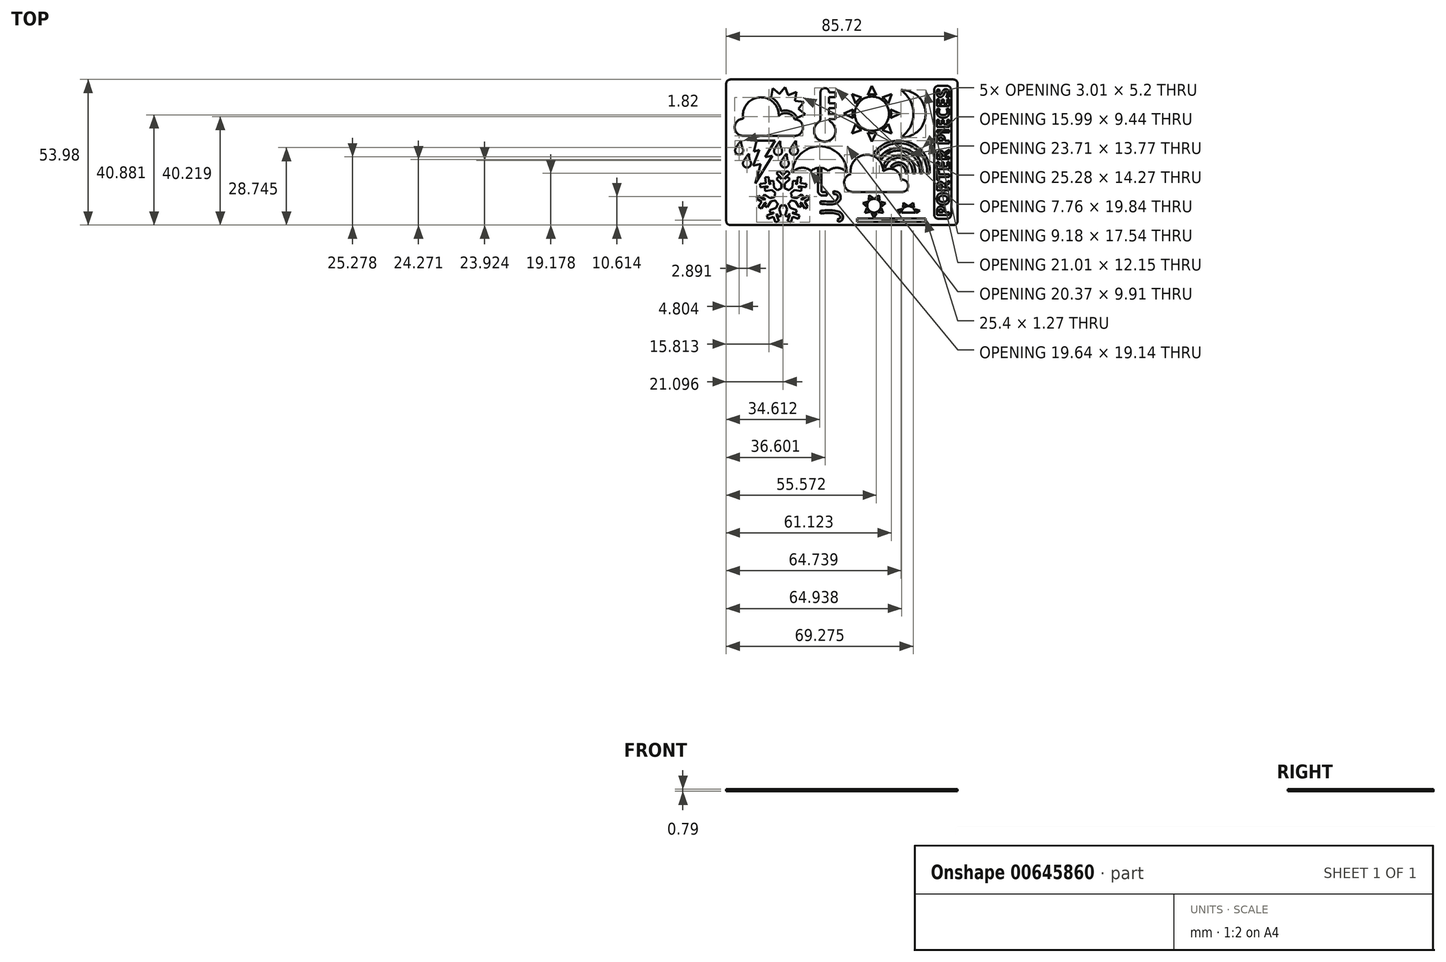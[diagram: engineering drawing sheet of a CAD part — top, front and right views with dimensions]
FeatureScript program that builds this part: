
annotation { "Feature Type Name" : "Feature", "Feature Type Description" : "" }
export const myFeature = defineFeature(function(context is Context, id is Id, definition is map)
    precondition{}
    {
        {
            var Q0;
            Q0=qCreatedBy(makeId("Top.planeOp"),FACE);
            var sketch = newSketch(context, id + "F0", { "sketchPlane" : qUnion([Q0])});
            skLineSegment(sketch, "E0.bottom", {"start": v(42.86, 26.99) * mm, "end": v(-42.86, 26.99) * mm});
            skLineSegment(sketch, "E0.top", {"start": v(42.86, -26.99) * mm, "end": v(-42.86, -26.99) * mm});
            skLineSegment(sketch, "E0.left", {"start": v(42.86, 26.99) * mm, "end": v(42.86, -26.99) * mm});
            skLineSegment(sketch, "E0.right", {"start": v(-42.86, 26.99) * mm, "end": v(-42.86, -26.99) * mm});
            skPoint(sketch, "E0.middle", {"position": v(0, 0) * mm});
            skSolve(sketch);
        }
        {
            var Q0;
            Q0=makeQuery(id+"F0.imprint","IMPRINT",FACE,{"disambiguationData":[TD([[makeQuery(id+"F0.imprint","IMPRINT",EDGE,{"derivedFrom":sQuery(id+"F0.wireOp",EDGE,"E0.bottom")}),1.0]])]});
            extrude(context, id + "F1", {"entities" : qUnion([Q0]), "depth" : 0.8 * mm, "offsetDistance" : 25.4 * mm});
        }
        {
            var Q0;
            Q0=makeQuery(id+"F1.opExtrude","SWEPT_EDGE",EDGE,{"disambiguationData":[OSD([sQuery(id+"F0.wireOp",EDGE,"E0.bottom"),sQuery(id+"F0.wireOp",EDGE,"E0.left")])]});
            var Q1;
            Q1=makeQuery(id+"F1.opExtrude","SWEPT_EDGE",EDGE,{"disambiguationData":[OSD([sQuery(id+"F0.wireOp",EDGE,"E0.bottom"),sQuery(id+"F0.wireOp",EDGE,"E0.right")])]});
            var Q2;
            Q2=makeQuery(id+"F1.opExtrude","SWEPT_EDGE",EDGE,{"disambiguationData":[OSD([sQuery(id+"F0.wireOp",EDGE,"E0.top"),sQuery(id+"F0.wireOp",EDGE,"E0.right")])]});
            var Q3;
            Q3=makeQuery(id+"F1.opExtrude","SWEPT_EDGE",EDGE,{"disambiguationData":[OSD([sQuery(id+"F0.wireOp",EDGE,"E0.top"),sQuery(id+"F0.wireOp",EDGE,"E0.left")])]});
            fillet(context, id + "F2", {"entities" : qUnion([Q0, Q1, Q2, Q3]), "radius" : 1.59 * mm, "tangentPropagation" : true, "allowEdgeOverflow" : false});
        }
        {
            var Q0;
            Q0=makeQuery(id+"F1.opExtrude","CAP_FACE",FACE,{"disambiguationData":[OSD([sQuery(id+"F0.wireOp",EDGE,"E0.bottom"),sQuery(id+"F0.wireOp",EDGE,"E0.top"),sQuery(id+"F0.wireOp",EDGE,"E0.left"),sQuery(id+"F0.wireOp",EDGE,"E0.right")])],"isStart":false});
            var sketch = newSketch(context, id + "F3", { "sketchPlane" : qUnion([Q0])});
            skLineSegment(sketch, "E1.bottom", {"start": v(34.13, -24.6) * mm, "end": v(40.48, -24.6) * mm});
            skLineSegment(sketch, "E1.top", {"start": v(34.13, 24.6) * mm, "end": v(40.48, 24.6) * mm});
            skLineSegment(sketch, "E1.left", {"start": v(34.13, -24.6) * mm, "end": v(34.13, 24.6) * mm});
            skLineSegment(sketch, "E1.right", {"start": v(40.48, -24.6) * mm, "end": v(40.48, 24.6) * mm});
            skSolve(sketch);
        }
        {
            var Q0;
            Q0=makeQuery(id+"F3.imprint","IMPRINT",FACE,{"disambiguationData":[TD([[makeQuery(id+"F3.imprint","IMPRINT",EDGE,{"derivedFrom":sQuery(id+"F3.wireOp",EDGE,"E1.bottom")}),1.0]])]});
            extrude(context, id + "F4", {"entities" : qUnion([Q0]), "operationType" : NewBodyOperationType.REMOVE, "oppositeDirection" : true, "depth" : 0.4 * mm, "offsetDistance" : 25.4 * mm});
        }
        {
            var Q0;
            Q0=makeQuery(id+"F4.boolean.opBoolean","COPY",EDGE,{"derivedFrom":makeQuery(id+"F4.opExtrude","SWEPT_EDGE",EDGE,{"disambiguationData":[OSD([sQuery(id+"F3.wireOp",EDGE,"E1.bottom"),sQuery(id+"F3.wireOp",EDGE,"E1.left")])]})});
            var Q1;
            Q1=makeQuery(id+"F4.boolean.opBoolean","COPY",EDGE,{"derivedFrom":makeQuery(id+"F4.opExtrude","SWEPT_EDGE",EDGE,{"disambiguationData":[OSD([sQuery(id+"F3.wireOp",EDGE,"E1.bottom"),sQuery(id+"F3.wireOp",EDGE,"E1.right")])]})});
            var Q2;
            Q2=makeQuery(id+"F4.boolean.opBoolean","COPY",EDGE,{"derivedFrom":makeQuery(id+"F4.opExtrude","SWEPT_EDGE",EDGE,{"disambiguationData":[OSD([sQuery(id+"F3.wireOp",EDGE,"E1.top"),sQuery(id+"F3.wireOp",EDGE,"E1.right")])]})});
            var Q3;
            Q3=makeQuery(id+"F4.boolean.opBoolean","COPY",EDGE,{"derivedFrom":makeQuery(id+"F4.opExtrude","SWEPT_EDGE",EDGE,{"disambiguationData":[OSD([sQuery(id+"F3.wireOp",EDGE,"E1.top"),sQuery(id+"F3.wireOp",EDGE,"E1.left")])]})});
            fillet(context, id + "F5", {"entities" : qUnion([Q0, Q1, Q2, Q3]), "radius" : 1.59 * mm, "tangentPropagation" : true, "allowEdgeOverflow" : false});
        }
        {
            var Q0;
            Q0=makeQuery(id+"F4.boolean.opBoolean","COPY",FACE,{"derivedFrom":makeQuery(id+"F4.opExtrude","CAP_FACE",FACE,{"disambiguationData":[OSD([sQuery(id+"F3.wireOp",EDGE,"E1.bottom"),sQuery(id+"F3.wireOp",EDGE,"E1.top"),sQuery(id+"F3.wireOp",EDGE,"E1.left"),sQuery(id+"F3.wireOp",EDGE,"E1.right")])],"isStart":false})});
            var sketch = newSketch(context, id + "F6", { "sketchPlane" : qUnion([Q0])});
            skText(sketch, "E2", { "text": "PORTER PIECES", "fontName": "OpenSans-Bold.ttf"});
            const initialGuessF6  = {"E2": [0.03976, -0.02381, 0, 1, 0.00461]};
            skSetInitialGuess(sketch, initialGuessF6);
            skSolve(sketch);
        }
        {
            var Q0;
            Q0=makeQuery(id+"F6.imprint","IMPRINT",FACE,{"disambiguationData":[TD([[makeQuery(id+"F6.imprint","IMPRINT",EDGE,{"derivedFrom":sQuery(id+"F6.wireOp",EDGE,"E2.sketch_text.stroke-0")}),-1.0]])]});
            var Q1;
            Q1=makeQuery(id+"F6.imprint","IMPRINT",FACE,{"disambiguationData":[TD([[makeQuery(id+"F6.imprint","IMPRINT",EDGE,{"derivedFrom":sQuery(id+"F6.wireOp",EDGE,"E2.sketch_text.stroke-16")}),-1.0]])]});
            var Q2;
            Q2=makeQuery(id+"F6.imprint","IMPRINT",FACE,{"disambiguationData":[TD([[makeQuery(id+"F6.imprint","IMPRINT",EDGE,{"derivedFrom":sQuery(id+"F6.wireOp",EDGE,"E2.sketch_text.stroke-30")}),-1.0]])]});
            var Q3;
            Q3=makeQuery(id+"F6.imprint","IMPRINT",FACE,{"disambiguationData":[TD([[makeQuery(id+"F6.imprint","IMPRINT",EDGE,{"derivedFrom":sQuery(id+"F6.wireOp",EDGE,"E2.sketch_text.stroke-49")}),-1.0]])]});
            var Q4;
            Q4=makeQuery(id+"F6.imprint","IMPRINT",FACE,{"disambiguationData":[TD([[makeQuery(id+"F6.imprint","IMPRINT",EDGE,{"derivedFrom":sQuery(id+"F6.wireOp",EDGE,"E2.sketch_text.stroke-57")}),-1.0]])]});
            var Q5;
            Q5=makeQuery(id+"F6.imprint","IMPRINT",FACE,{"disambiguationData":[TD([[makeQuery(id+"F6.imprint","IMPRINT",EDGE,{"derivedFrom":sQuery(id+"F6.wireOp",EDGE,"E2.sketch_text.stroke-69")}),-1.0]])]});
            var Q6;
            Q6=makeQuery(id+"F6.imprint","IMPRINT",FACE,{"disambiguationData":[TD([[makeQuery(id+"F6.imprint","IMPRINT",EDGE,{"derivedFrom":sQuery(id+"F6.wireOp",EDGE,"E2.sketch_text.stroke-88")}),-1.0]])]});
            var Q7;
            Q7=makeQuery(id+"F6.imprint","IMPRINT",FACE,{"disambiguationData":[TD([[makeQuery(id+"F6.imprint","IMPRINT",EDGE,{"derivedFrom":sQuery(id+"F6.wireOp",EDGE,"E2.sketch_text.stroke-104")}),-1.0]])]});
            var Q8;
            Q8=makeQuery(id+"F6.imprint","IMPRINT",FACE,{"disambiguationData":[TD([[makeQuery(id+"F6.imprint","IMPRINT",EDGE,{"derivedFrom":sQuery(id+"F6.wireOp",EDGE,"E2.sketch_text.stroke-108")}),-1.0]])]});
            var Q9;
            Q9=makeQuery(id+"F6.imprint","IMPRINT",FACE,{"disambiguationData":[TD([[makeQuery(id+"F6.imprint","IMPRINT",EDGE,{"derivedFrom":sQuery(id+"F6.wireOp",EDGE,"E2.sketch_text.stroke-120")}),-1.0]])]});
            var Q10;
            Q10=makeQuery(id+"F6.imprint","IMPRINT",FACE,{"disambiguationData":[TD([[makeQuery(id+"F6.imprint","IMPRINT",EDGE,{"derivedFrom":sQuery(id+"F6.wireOp",EDGE,"E2.sketch_text.stroke-135")}),-1.0]])]});
            var Q11;
            Q11=makeQuery(id+"F6.imprint","IMPRINT",FACE,{"disambiguationData":[TD([[makeQuery(id+"F6.imprint","IMPRINT",EDGE,{"derivedFrom":sQuery(id+"F6.wireOp",EDGE,"E2.sketch_text.stroke-147")}),-1.0]])]});
            extrude(context, id + "F7", {"entities" : qUnion([Q0, Q1, Q2, Q3, Q4, Q5, Q6, Q7, Q8, Q9, Q10, Q11]), "operationType" : NewBodyOperationType.ADD, "depth" : 0.4 * mm, "offsetDistance" : 25.4 * mm});
        }
        {
            var Q0;
            Q0=makeQuery(id+"F1.opExtrude","CAP_FACE",FACE,{"disambiguationData":[OSD([sQuery(id+"F0.wireOp",EDGE,"E0.bottom"),sQuery(id+"F0.wireOp",EDGE,"E0.top"),sQuery(id+"F0.wireOp",EDGE,"E0.left"),sQuery(id+"F0.wireOp",EDGE,"E0.right")])],"isStart":false});
            var sketch = newSketch(context, id + "F8", { "sketchPlane" : qUnion([Q0])});
            skLineSegment(sketch, "E3", {"start": v(-36.52, 6.1) * mm, "end": v(-17.47, 6.1) * mm});
            skArc(sketch, "E4", {"start": v(-36.52, 12.44) * mm, "mid": v(-39.69, 9.27) * mm, "end": v(-36.52, 6.1) * mm});
            skArc(sketch, "E5", {"start": v(-17.47, 6.1) * mm, "mid": v(-14.4, 9.16) * mm, "end": v(-17.47, 12.22) * mm});
            skArc(sketch, "E6", {"start": v(-23.4, 13.5) * mm, "mid": v(-30.55, 20.36) * mm, "end": v(-36.52, 12.44) * mm});
            skArc(sketch, "E7", {"start": v(-17.47, 12.22) * mm, "mid": v(-20.1, 14.42) * mm, "end": v(-23.4, 13.5) * mm});
            skSolve(sketch);
        }
        {
            var Q0;
            Q0=makeQuery(id+"F8.imprint","IMPRINT",FACE,{"disambiguationData":[TD([[makeQuery(id+"F8.imprint","IMPRINT",EDGE,{"derivedFrom":sQuery(id+"F8.wireOp",EDGE,"E3")}),1.0]])]});
            extrude(context, id + "F9", {"entities" : qUnion([Q0]), "operationType" : NewBodyOperationType.REMOVE, "oppositeDirection" : true, "depth" : 25.4 * mm, "offsetDistance" : 25.4 * mm});
        }
        {
            var Q0;
            Q0=makeQuery(id+"F1.opExtrude","CAP_FACE",FACE,{"disambiguationData":[OSD([sQuery(id+"F0.wireOp",EDGE,"E0.bottom"),sQuery(id+"F0.wireOp",EDGE,"E0.top"),sQuery(id+"F0.wireOp",EDGE,"E0.left"),sQuery(id+"F0.wireOp",EDGE,"E0.right")])],"isStart":false});
            var sketch = newSketch(context, id + "F10", { "sketchPlane" : qUnion([Q0])});
            skArc(sketch, "E8.0", {"start": v(-22.52, 15.22) * mm, "mid": v(-23.87, 18.3) * mm, "end": v(-26.4, 20.49) * mm});
            skArc(sketch, "E9.0", {"start": v(-16.53, 12.6) * mm, "mid": v(-19, 15.13) * mm, "end": v(-22.52, 15.22) * mm});
            skPoint(sketch, "E10", {"position": v(-22.52, 15.22) * mm});
            skArc(sketch, "E11", {"start": v(-16.53, 12.6) * mm, "mid": v(-18.44, 20.33) * mm, "end": v(-26.4, 20.49) * mm});
            skSolve(sketch);
        }
        {
            var Q0;
            Q0=makeQuery(id+"F10.imprint","IMPRINT",FACE,{"disambiguationData":[TD([[makeQuery(id+"F10.imprint","IMPRINT",EDGE,{"derivedFrom":sQuery(id+"F10.wireOp",EDGE,"E8.0")}),-1.0]])]});
            extrude(context, id + "F11", {"entities" : qUnion([Q0]), "operationType" : NewBodyOperationType.REMOVE, "oppositeDirection" : true, "depth" : 25.4 * mm, "offsetDistance" : 25.4 * mm});
        }
        {
            var Q0;
            Q0=makeQuery(id+"F1.opExtrude","CAP_FACE",FACE,{"disambiguationData":[OSD([sQuery(id+"F0.wireOp",EDGE,"E0.bottom"),sQuery(id+"F0.wireOp",EDGE,"E0.top"),sQuery(id+"F0.wireOp",EDGE,"E0.left"),sQuery(id+"F0.wireOp",EDGE,"E0.right")])],"isStart":false});
            var sketch = newSketch(context, id + "F12", { "sketchPlane" : qUnion([Q0])});
            skLineSegment(sketch, "E12", {"start": v(-22.52, 15.22) * mm, "end": v(-26.8, 26.99) * mm, "construction": true});
            skCircle(sketch, "E13", {"center": v(-22.52, 15.22) * mm, "radius": 9.08 * mm, "construction": true});
            skLineSegment(sketch, "E14", {"start": v(-25.63, 23.76) * mm, "end": v(-26.2, 20.5) * mm});
            skCircle(sketch, "E15", {"center": v(-25.63, 23.76) * mm, "radius": 3.3 * mm, "construction": true});
            skLineSegment(sketch, "E16", {"start": v(-25.63, 23.76) * mm, "end": v(-23.1, 21.63) * mm});
            skLineSegment(sketch, "E17", {"start": v(-23.1, 21.63) * mm, "end": v(-26.2, 20.5) * mm});
            skLineSegment(sketch, "E18.1.0", {"start": v(-21.04, 24.18) * mm, "end": v(-19.88, 21.1) * mm});
            skLineSegment(sketch, "E18.1.1", {"start": v(-21.04, 24.18) * mm, "end": v(-23.14, 21.63) * mm});
            skLineSegment(sketch, "E18.1.2", {"start": v(-19.88, 21.1) * mm, "end": v(-23.14, 21.63) * mm});
            skLineSegment(sketch, "E18.2.0", {"start": v(-16.83, 22.3) * mm, "end": v(-17.34, 19.04) * mm});
            skLineSegment(sketch, "E18.2.1", {"start": v(-16.83, 22.3) * mm, "end": v(-19.91, 21.1) * mm});
            skLineSegment(sketch, "E18.2.2", {"start": v(-17.34, 19.04) * mm, "end": v(-19.91, 21.1) * mm});
            skLineSegment(sketch, "E18.3.0", {"start": v(-14.1, 18.6) * mm, "end": v(-16.13, 16) * mm});
            skLineSegment(sketch, "E18.3.1", {"start": v(-14.1, 18.6) * mm, "end": v(-17.36, 19.07) * mm});
            skLineSegment(sketch, "E18.3.2", {"start": v(-16.13, 16) * mm, "end": v(-17.36, 19.07) * mm});
            skLineSegment(sketch, "E18.4.0", {"start": v(-13.52, 14.03) * mm, "end": v(-16.57, 12.77) * mm});
            skLineSegment(sketch, "E18.4.1", {"start": v(-13.52, 14.03) * mm, "end": v(-16.14, 16.04) * mm});
            skLineSegment(sketch, "E18.4.2", {"start": v(-16.57, 12.77) * mm, "end": v(-16.14, 16.04) * mm});
            skLineSegment(sketch, "E18.anchor1", {"start": v(-22.52, 15.22) * mm, "end": v(-26.2, 20.5) * mm, "construction": true});
            skLineSegment(sketch, "E18.anchor2", {"start": v(-22.52, 15.22) * mm, "end": v(-16.14, 16.04) * mm, "construction": true});
            skSolve(sketch);
        }
        {
            var Q0;
            {var subQ0=sQuery(id+"F12.wireOp",EDGE,"E18.1.1");var subQ1=sQuery(id+"F12.wireOp",EDGE,"E18.1.0");var subQ2=makeQuery(id+"F12.imprint","INTERSECT",VERTEX,{"derivedFrom":[subQ1,subQ0]});Q0=makeQuery(id+"F12.imprint","IMPRINT",FACE,{"disambiguationData":[TD([[makeQuery(id+"F12.imprint","IMPRINT",EDGE,{"disambiguationData":[TD([[subQ2,-1.0]])],"derivedFrom":subQ1}),-1.0]])]});}
            var Q1;
            {var subQ0=sQuery(id+"F12.wireOp",EDGE,"E18.2.1");var subQ1=sQuery(id+"F12.wireOp",EDGE,"E18.2.0");var subQ2=makeQuery(id+"F12.imprint","INTERSECT",VERTEX,{"derivedFrom":[subQ1,subQ0]});Q1=makeQuery(id+"F12.imprint","IMPRINT",FACE,{"disambiguationData":[TD([[makeQuery(id+"F12.imprint","IMPRINT",EDGE,{"disambiguationData":[TD([[subQ2,-1.0]])],"derivedFrom":subQ1}),-1.0]])]});}
            var Q2;
            {var subQ0=sQuery(id+"F12.wireOp",EDGE,"E18.3.1");var subQ1=sQuery(id+"F12.wireOp",EDGE,"E18.3.0");var subQ2=makeQuery(id+"F12.imprint","INTERSECT",VERTEX,{"derivedFrom":[subQ1,subQ0]});Q2=makeQuery(id+"F12.imprint","IMPRINT",FACE,{"disambiguationData":[TD([[makeQuery(id+"F12.imprint","IMPRINT",EDGE,{"disambiguationData":[TD([[subQ2,-1.0]])],"derivedFrom":subQ1}),-1.0]])]});}
            var Q3;
            {var subQ0=sQuery(id+"F12.wireOp",EDGE,"E18.4.1");var subQ1=sQuery(id+"F12.wireOp",EDGE,"E18.4.0");var subQ2=makeQuery(id+"F12.imprint","INTERSECT",VERTEX,{"derivedFrom":[subQ1,subQ0]});Q3=makeQuery(id+"F12.imprint","IMPRINT",FACE,{"disambiguationData":[TD([[makeQuery(id+"F12.imprint","IMPRINT",EDGE,{"disambiguationData":[TD([[subQ2,-1.0]])],"derivedFrom":subQ1}),-1.0]])]});}
            var Q4;
            {var subQ0=sQuery(id+"F12.wireOp",EDGE,"E16");var subQ1=sQuery(id+"F12.wireOp",EDGE,"E14");var subQ2=makeQuery(id+"F12.imprint","INTERSECT",VERTEX,{"derivedFrom":[subQ1,subQ0]});Q4=makeQuery(id+"F12.imprint","IMPRINT",FACE,{"disambiguationData":[TD([[makeQuery(id+"F12.imprint","IMPRINT",EDGE,{"disambiguationData":[TD([[subQ2,-1.0]])],"derivedFrom":subQ1}),1.0]])]});}
            extrude(context, id + "F13", {"entities" : qUnion([Q0, Q1, Q2, Q3, Q4]), "operationType" : NewBodyOperationType.REMOVE, "oppositeDirection" : true, "depth" : 25.4 * mm, "offsetDistance" : 25.4 * mm});
        }
        {
            var Q0;
            Q0=makeQuery(id+"F1.opExtrude","CAP_FACE",FACE,{"disambiguationData":[OSD([sQuery(id+"F0.wireOp",EDGE,"E0.bottom"),sQuery(id+"F0.wireOp",EDGE,"E0.top"),sQuery(id+"F0.wireOp",EDGE,"E0.left"),sQuery(id+"F0.wireOp",EDGE,"E0.right")])],"isStart":false});
            var sketch = newSketch(context, id + "F14", { "sketchPlane" : qUnion([Q0])});
            skLineSegment(sketch, "E19", {"start": v(-31.65, 4.32) * mm, "end": v(-24.78, 4.32) * mm});
            skLineSegment(sketch, "E20", {"start": v(-24.78, 4.32) * mm, "end": v(-28.4, -1.8) * mm});
            skLineSegment(sketch, "E21", {"start": v(-28.4, -1.8) * mm, "end": v(-25.75, -1.3) * mm});
            skLineSegment(sketch, "E22", {"start": v(-25.75, -1.3) * mm, "end": v(-32.04, -11.58) * mm});
            skLineSegment(sketch, "E23", {"start": v(-32.04, -11.58) * mm, "end": v(-30.12, -4.3) * mm});
            skLineSegment(sketch, "E24", {"start": v(-30.12, -4.3) * mm, "end": v(-32.9, -4.9) * mm});
            skLineSegment(sketch, "E25", {"start": v(-32.9, -4.9) * mm, "end": v(-30.52, 0.86) * mm});
            skLineSegment(sketch, "E26", {"start": v(-30.52, 0.86) * mm, "end": v(-32.6, 0.2) * mm});
            skLineSegment(sketch, "E27", {"start": v(-32.6, 0.2) * mm, "end": v(-31.65, 4.32) * mm});
            skSolve(sketch);
        }
        {
            var Q0;
            Q0=makeQuery(id+"F14.imprint","IMPRINT",FACE,{"disambiguationData":[TD([[makeQuery(id+"F14.imprint","IMPRINT",EDGE,{"derivedFrom":sQuery(id+"F14.wireOp",EDGE,"E19")}),-1.0]])]});
            extrude(context, id + "F15", {"entities" : qUnion([Q0]), "operationType" : NewBodyOperationType.REMOVE, "oppositeDirection" : true, "depth" : 25.4 * mm, "offsetDistance" : 25.4 * mm});
        }
        {
            var Q0;
            Q0=makeQuery(id+"F1.opExtrude","CAP_FACE",FACE,{"disambiguationData":[OSD([sQuery(id+"F0.wireOp",EDGE,"E0.bottom"),sQuery(id+"F0.wireOp",EDGE,"E0.top"),sQuery(id+"F0.wireOp",EDGE,"E0.left"),sQuery(id+"F0.wireOp",EDGE,"E0.right")])],"isStart":false});
            var sketch = newSketch(context, id + "F16", { "sketchPlane" : qUnion([Q0])});
            skArc(sketch, "E28", {"start": v(-39.4, 1.35) * mm, "mid": v(-38.08, -0.85) * mm, "end": v(-36.7, 1.3) * mm});
            skArc(sketch, "E29", {"start": v(-39.4, 1.35) * mm, "mid": v(-38.44, 2.92) * mm, "end": v(-37.3, 4.36) * mm});
            skArc(sketch, "E30", {"start": v(-37.3, 4.36) * mm, "mid": v(-37.19, 2.8) * mm, "end": v(-36.7, 1.3) * mm});
            skArc(sketch, "E31", {"start": v(-24.98, 1.15) * mm, "mid": v(-23.66, -1.05) * mm, "end": v(-22.28, 1.1) * mm});
            skArc(sketch, "E32", {"start": v(-24.98, 1.15) * mm, "mid": v(-24.03, 2.72) * mm, "end": v(-22.88, 4.16) * mm});
            skArc(sketch, "E33", {"start": v(-22.88, 4.16) * mm, "mid": v(-22.77, 2.6) * mm, "end": v(-22.28, 1.1) * mm});
            skArc(sketch, "E34", {"start": v(-22.52, -3.47) * mm, "mid": v(-21.2, -5.66) * mm, "end": v(-19.82, -3.5) * mm});
            skArc(sketch, "E35", {"start": v(-22.52, -3.47) * mm, "mid": v(-21.57, -1.9) * mm, "end": v(-20.41, -0.46) * mm});
            skArc(sketch, "E36", {"start": v(-20.41, -0.46) * mm, "mid": v(-20.31, -2.02) * mm, "end": v(-19.82, -3.5) * mm});
            skArc(sketch, "E37", {"start": v(-19.1, 1.26) * mm, "mid": v(-17.8, -0.94) * mm, "end": v(-16.41, 1.22) * mm});
            skArc(sketch, "E38", {"start": v(-19.1, 1.26) * mm, "mid": v(-18.15, 2.83) * mm, "end": v(-17, 4.26) * mm});
            skArc(sketch, "E39", {"start": v(-17, 4.26) * mm, "mid": v(-16.9, 2.7) * mm, "end": v(-16.41, 1.22) * mm});
            skArc(sketch, "E40", {"start": v(-36.5, -3.47) * mm, "mid": v(-35.19, -5.66) * mm, "end": v(-33.8, -3.5) * mm});
            skArc(sketch, "E41", {"start": v(-36.5, -3.47) * mm, "mid": v(-35.55, -1.9) * mm, "end": v(-34.4, -0.46) * mm});
            skArc(sketch, "E42", {"start": v(-34.4, -0.46) * mm, "mid": v(-34.3, -2.02) * mm, "end": v(-33.8, -3.5) * mm});
            skSolve(sketch);
        }
        {
            var Q0;
            Q0=makeQuery(id+"F16.imprint","IMPRINT",FACE,{"disambiguationData":[TD([[makeQuery(id+"F16.imprint","IMPRINT",EDGE,{"derivedFrom":sQuery(id+"F16.wireOp",EDGE,"E28")}),1.0]])]});
            var Q1;
            Q1=makeQuery(id+"F16.imprint","IMPRINT",FACE,{"disambiguationData":[TD([[makeQuery(id+"F16.imprint","IMPRINT",EDGE,{"derivedFrom":sQuery(id+"F16.wireOp",EDGE,"E40")}),1.0]])]});
            var Q2;
            Q2=makeQuery(id+"F16.imprint","IMPRINT",FACE,{"disambiguationData":[TD([[makeQuery(id+"F16.imprint","IMPRINT",EDGE,{"derivedFrom":sQuery(id+"F16.wireOp",EDGE,"E31")}),1.0]])]});
            var Q3;
            Q3=makeQuery(id+"F16.imprint","IMPRINT",FACE,{"disambiguationData":[TD([[makeQuery(id+"F16.imprint","IMPRINT",EDGE,{"derivedFrom":sQuery(id+"F16.wireOp",EDGE,"E34")}),1.0]])]});
            var Q4;
            Q4=makeQuery(id+"F16.imprint","IMPRINT",FACE,{"disambiguationData":[TD([[makeQuery(id+"F16.imprint","IMPRINT",EDGE,{"derivedFrom":sQuery(id+"F16.wireOp",EDGE,"E37")}),1.0]])]});
            extrude(context, id + "F17", {"entities" : qUnion([Q0, Q1, Q2, Q3, Q4]), "operationType" : NewBodyOperationType.REMOVE, "oppositeDirection" : true, "depth" : 25.4 * mm, "offsetDistance" : 25.4 * mm});
        }
        {
            var Q0;
            Q0=makeQuery(id+"F1.opExtrude","CAP_FACE",FACE,{"disambiguationData":[OSD([sQuery(id+"F0.wireOp",EDGE,"E0.bottom"),sQuery(id+"F0.wireOp",EDGE,"E0.top"),sQuery(id+"F0.wireOp",EDGE,"E0.left"),sQuery(id+"F0.wireOp",EDGE,"E0.right")])],"isStart":false});
            var sketch = newSketch(context, id + "F18", { "sketchPlane" : qUnion([Q0])});
            skLineSegment(sketch, "E43.bottom", {"start": v(-7.94, 23.81) * mm, "end": v(-4.76, 23.81) * mm});
            skLineSegment(sketch, "E43.top", {"start": v(-7.94, 7.94) * mm, "end": v(-4.76, 7.94) * mm});
            skLineSegment(sketch, "E43.left", {"start": v(-7.94, 23.81) * mm, "end": v(-7.94, 7.94) * mm});
            skLineSegment(sketch, "E43.right", {"start": v(-4.76, 23.81) * mm, "end": v(-4.76, 7.94) * mm});
            skCircle(sketch, "E44", {"center": v(-6.35, 7.94) * mm, "radius": 3.97 * mm});
            skSolve(sketch);
        }
        {
            var Q0;
            {var subQ0=sQuery(id+"F18.wireOp",EDGE,"E43.bottom");Q0=makeQuery(id+"F18.imprint","IMPRINT",FACE,{"disambiguationData":[TD([[makeQuery(id+"F18.imprint","IMPRINT",EDGE,{"derivedFrom":subQ0}),-1.0]])]});}
            var Q1;
            {var subQ0=sQuery(id+"F18.wireOp",EDGE,"E43.top");Q1=makeQuery(id+"F18.imprint","IMPRINT",FACE,{"disambiguationData":[TD([[makeQuery(id+"F18.imprint","IMPRINT",EDGE,{"derivedFrom":subQ0}),1.0]])]});}
            var Q2;
            {var subQ0=sQuery(id+"F18.wireOp",EDGE,"E43.top");Q2=makeQuery(id+"F18.imprint","IMPRINT",FACE,{"disambiguationData":[TD([[makeQuery(id+"F18.imprint","IMPRINT",EDGE,{"derivedFrom":subQ0}),-1.0]])]});}
            extrude(context, id + "F19", {"entities" : qUnion([Q0, Q1, Q2]), "operationType" : NewBodyOperationType.REMOVE, "oppositeDirection" : true, "depth" : 25.4 * mm, "offsetDistance" : 25.4 * mm});
        }
        {
            var Q0;
            Q0=makeQuery(id+"F19.boolean.opBoolean","COPY",EDGE,{"derivedFrom":makeQuery(id+"F19.opExtrude","SWEPT_EDGE",EDGE,{"disambiguationData":[OSD([sQuery(id+"F18.wireOp",EDGE,"E43.left"),sQuery(id+"F18.wireOp",EDGE,"E44")])]})});
            var Q1;
            Q1=makeQuery(id+"F19.boolean.opBoolean","COPY",EDGE,{"derivedFrom":makeQuery(id+"F19.opExtrude","SWEPT_EDGE",EDGE,{"disambiguationData":[OSD([sQuery(id+"F18.wireOp",EDGE,"E43.right"),sQuery(id+"F18.wireOp",EDGE,"E44")])]})});
            fillet(context, id + "F20", {"entities" : qUnion([Q0, Q1]), "radius" : 1.59 * mm, "tangentPropagation" : true, "allowEdgeOverflow" : false});
        }
        {
            var Q0;
            Q0=makeQuery(id+"F19.boolean.opBoolean","COPY",EDGE,{"derivedFrom":makeQuery(id+"F19.opExtrude","SWEPT_EDGE",EDGE,{"disambiguationData":[OSD([sQuery(id+"F18.wireOp",EDGE,"E43.bottom"),sQuery(id+"F18.wireOp",EDGE,"E43.right")])]})});
            var Q1;
            Q1=makeQuery(id+"F19.boolean.opBoolean","COPY",EDGE,{"derivedFrom":makeQuery(id+"F19.opExtrude","SWEPT_EDGE",EDGE,{"disambiguationData":[OSD([sQuery(id+"F18.wireOp",EDGE,"E43.bottom"),sQuery(id+"F18.wireOp",EDGE,"E43.left")])]})});
            fillet(context, id + "F21", {"entities" : qUnion([Q0, Q1]), "radius" : 1.59 * mm, "tangentPropagation" : true, "allowEdgeOverflow" : false});
        }
        {
            var Q0;
            Q0=makeQuery(id+"F1.opExtrude","CAP_FACE",FACE,{"disambiguationData":[OSD([sQuery(id+"F0.wireOp",EDGE,"E0.bottom"),sQuery(id+"F0.wireOp",EDGE,"E0.top"),sQuery(id+"F0.wireOp",EDGE,"E0.left"),sQuery(id+"F0.wireOp",EDGE,"E0.right")])],"isStart":false});
            var sketch = newSketch(context, id + "F22", { "sketchPlane" : qUnion([Q0])});
            skLineSegment(sketch, "E45.bottom", {"start": v(-4.76, 22.23) * mm, "end": v(-2.38, 22.23) * mm});
            skLineSegment(sketch, "E45.top", {"start": v(-4.76, 20.45) * mm, "end": v(-2.38, 20.45) * mm});
            skLineSegment(sketch, "E45.left", {"start": v(-4.76, 22.23) * mm, "end": v(-4.76, 20.45) * mm});
            skLineSegment(sketch, "E45.right", {"start": v(-2.38, 22.23) * mm, "end": v(-2.38, 20.45) * mm});
            skLineSegment(sketch, "E46.bottom", {"start": v(-4.76, 18.16) * mm, "end": v(-2.38, 18.16) * mm});
            skLineSegment(sketch, "E46.top", {"start": v(-4.76, 16.38) * mm, "end": v(-2.38, 16.38) * mm});
            skLineSegment(sketch, "E46.left", {"start": v(-4.76, 18.16) * mm, "end": v(-4.76, 16.38) * mm});
            skLineSegment(sketch, "E46.right", {"start": v(-2.38, 18.16) * mm, "end": v(-2.38, 16.38) * mm});
            skLineSegment(sketch, "E47.bottom", {"start": v(-4.76, 14.1) * mm, "end": v(-2.38, 14.1) * mm});
            skLineSegment(sketch, "E47.top", {"start": v(-4.76, 12.32) * mm, "end": v(-2.38, 12.32) * mm});
            skLineSegment(sketch, "E47.left", {"start": v(-4.76, 14.1) * mm, "end": v(-4.76, 12.32) * mm});
            skLineSegment(sketch, "E47.right", {"start": v(-2.38, 14.1) * mm, "end": v(-2.38, 12.32) * mm});
            skSolve(sketch);
        }
        {
            var Q0;
            Q0=makeQuery(id+"F22.imprint","IMPRINT",FACE,{"disambiguationData":[TD([[makeQuery(id+"F22.imprint","IMPRINT",EDGE,{"derivedFrom":sQuery(id+"F22.wireOp",EDGE,"E45.bottom")}),-1.0]])]});
            var Q1;
            Q1=makeQuery(id+"F22.imprint","IMPRINT",FACE,{"disambiguationData":[TD([[makeQuery(id+"F22.imprint","IMPRINT",EDGE,{"derivedFrom":sQuery(id+"F22.wireOp",EDGE,"E46.bottom")}),-1.0]])]});
            var Q2;
            Q2=makeQuery(id+"F22.imprint","IMPRINT",FACE,{"disambiguationData":[TD([[makeQuery(id+"F22.imprint","IMPRINT",EDGE,{"derivedFrom":sQuery(id+"F22.wireOp",EDGE,"E47.bottom")}),-1.0]])]});
            extrude(context, id + "F23", {"entities" : qUnion([Q0, Q1, Q2]), "operationType" : NewBodyOperationType.REMOVE, "oppositeDirection" : true, "depth" : 25.4 * mm, "offsetDistance" : 25.4 * mm});
        }
        {
            var Q0;
            Q0=makeQuery(id+"F1.opExtrude","CAP_FACE",FACE,{"disambiguationData":[OSD([sQuery(id+"F0.wireOp",EDGE,"E0.bottom"),sQuery(id+"F0.wireOp",EDGE,"E0.top"),sQuery(id+"F0.wireOp",EDGE,"E0.left"),sQuery(id+"F0.wireOp",EDGE,"E0.right")])],"isStart":false});
            var sketch = newSketch(context, id + "F24", { "sketchPlane" : qUnion([Q0])});
            skCircle(sketch, "E48", {"center": v(11.11, 14.29) * mm, "radius": 6.35 * mm});
            skSolve(sketch);
        }
        {
            var Q0;
            Q0=makeQuery(id+"F24.imprint","IMPRINT",FACE,{"disambiguationData":[TD([[makeQuery(id+"F24.imprint","IMPRINT",EDGE,{"derivedFrom":sQuery(id+"F24.wireOp",EDGE,"E48")}),1.0]])]});
            extrude(context, id + "F25", {"entities" : qUnion([Q0]), "operationType" : NewBodyOperationType.REMOVE, "oppositeDirection" : true, "depth" : 25.4 * mm, "offsetDistance" : 25.4 * mm});
        }
        {
            var Q0;
            Q0=makeQuery(id+"F1.opExtrude","CAP_FACE",FACE,{"disambiguationData":[OSD([sQuery(id+"F0.wireOp",EDGE,"E0.bottom"),sQuery(id+"F0.wireOp",EDGE,"E0.top"),sQuery(id+"F0.wireOp",EDGE,"E0.left"),sQuery(id+"F0.wireOp",EDGE,"E0.right")])],"isStart":false});
            var sketch = newSketch(context, id + "F26", { "sketchPlane" : qUnion([Q0])});
            skArc(sketch, "E49", {"start": v(12.72, 21.25) * mm, "mid": v(11.11, 21.43) * mm, "end": v(9.5, 21.25) * mm});
            skLineSegment(sketch, "E50", {"start": v(11.11, 14.29) * mm, "end": v(11.11, 24.7) * mm, "construction": true});
            skLineSegment(sketch, "E51", {"start": v(11.11, 24.7) * mm, "end": v(9.5, 21.25) * mm});
            skLineSegment(sketch, "E52", {"start": v(11.11, 24.7) * mm, "end": v(12.72, 21.25) * mm});
            skLineSegment(sketch, "E53.1.0", {"start": v(3.76, 21.64) * mm, "end": v(7.32, 20.35) * mm});
            skLineSegment(sketch, "E53.1.1", {"start": v(3.76, 21.64) * mm, "end": v(5.05, 18.08) * mm});
            skArc(sketch, "E53.1.2", {"start": v(7.32, 20.35) * mm, "mid": v(6.06, 19.34) * mm, "end": v(5.05, 18.08) * mm});
            skLineSegment(sketch, "E53.1.3", {"start": v(11.11, 14.29) * mm, "end": v(3.76, 21.64) * mm, "construction": true});
            skLineSegment(sketch, "E53.2.0", {"start": v(0.7, 14.29) * mm, "end": v(4.15, 15.9) * mm});
            skLineSegment(sketch, "E53.2.1", {"start": v(0.7, 14.29) * mm, "end": v(4.15, 12.68) * mm});
            skArc(sketch, "E53.2.2", {"start": v(4.15, 15.9) * mm, "mid": v(3.97, 14.29) * mm, "end": v(4.15, 12.68) * mm});
            skLineSegment(sketch, "E53.2.3", {"start": v(11.11, 14.29) * mm, "end": v(0.7, 14.29) * mm, "construction": true});
            skLineSegment(sketch, "E53.3.0", {"start": v(3.76, 6.93) * mm, "end": v(5.05, 10.5) * mm});
            skLineSegment(sketch, "E53.3.1", {"start": v(3.76, 6.93) * mm, "end": v(7.32, 8.23) * mm});
            skArc(sketch, "E53.3.2", {"start": v(5.05, 10.5) * mm, "mid": v(6.06, 9.23) * mm, "end": v(7.32, 8.23) * mm});
            skLineSegment(sketch, "E53.3.3", {"start": v(11.11, 14.29) * mm, "end": v(3.76, 6.93) * mm, "construction": true});
            skLineSegment(sketch, "E53.4.0", {"start": v(11.11, 3.88) * mm, "end": v(9.5, 7.32) * mm});
            skLineSegment(sketch, "E53.4.1", {"start": v(11.11, 3.88) * mm, "end": v(12.72, 7.32) * mm});
            skArc(sketch, "E53.4.2", {"start": v(9.5, 7.32) * mm, "mid": v(11.11, 7.14) * mm, "end": v(12.72, 7.32) * mm});
            skLineSegment(sketch, "E53.4.3", {"start": v(11.11, 14.29) * mm, "end": v(11.11, 3.88) * mm, "construction": true});
            skLineSegment(sketch, "E53.5.0", {"start": v(18.47, 6.93) * mm, "end": v(14.9, 8.23) * mm});
            skLineSegment(sketch, "E53.5.1", {"start": v(18.47, 6.93) * mm, "end": v(17.17, 10.5) * mm});
            skArc(sketch, "E53.5.2", {"start": v(14.9, 8.23) * mm, "mid": v(16.17, 9.23) * mm, "end": v(17.17, 10.5) * mm});
            skLineSegment(sketch, "E53.5.3", {"start": v(11.11, 14.29) * mm, "end": v(18.47, 6.93) * mm, "construction": true});
            skLineSegment(sketch, "E53.6.0", {"start": v(21.52, 14.29) * mm, "end": v(18.08, 12.68) * mm});
            skLineSegment(sketch, "E53.6.1", {"start": v(21.52, 14.29) * mm, "end": v(18.08, 15.9) * mm});
            skArc(sketch, "E53.6.2", {"start": v(18.08, 12.68) * mm, "mid": v(18.26, 14.29) * mm, "end": v(18.08, 15.9) * mm});
            skLineSegment(sketch, "E53.6.3", {"start": v(11.11, 14.29) * mm, "end": v(21.52, 14.29) * mm, "construction": true});
            skLineSegment(sketch, "E53.7.0", {"start": v(18.47, 21.64) * mm, "end": v(17.17, 18.08) * mm});
            skLineSegment(sketch, "E53.7.1", {"start": v(18.47, 21.64) * mm, "end": v(14.9, 20.35) * mm});
            skArc(sketch, "E53.7.2", {"start": v(17.17, 18.08) * mm, "mid": v(16.17, 19.34) * mm, "end": v(14.9, 20.35) * mm});
            skLineSegment(sketch, "E53.7.3", {"start": v(11.11, 14.29) * mm, "end": v(18.47, 21.64) * mm, "construction": true});
            skSolve(sketch);
        }
        {
            var Q0;
            Q0=makeQuery(id+"F26.imprint","IMPRINT",FACE,{"disambiguationData":[TD([[makeQuery(id+"F26.imprint","IMPRINT",EDGE,{"derivedFrom":sQuery(id+"F26.wireOp",EDGE,"E49")}),-1.0]])]});
            var Q1;
            Q1=makeQuery(id+"F26.imprint","IMPRINT",FACE,{"disambiguationData":[TD([[makeQuery(id+"F26.imprint","IMPRINT",EDGE,{"derivedFrom":sQuery(id+"F26.wireOp",EDGE,"E53.1.0")}),-1.0]])]});
            var Q2;
            Q2=makeQuery(id+"F26.imprint","IMPRINT",FACE,{"disambiguationData":[TD([[makeQuery(id+"F26.imprint","IMPRINT",EDGE,{"derivedFrom":sQuery(id+"F26.wireOp",EDGE,"E53.2.0")}),-1.0]])]});
            var Q3;
            Q3=makeQuery(id+"F26.imprint","IMPRINT",FACE,{"disambiguationData":[TD([[makeQuery(id+"F26.imprint","IMPRINT",EDGE,{"derivedFrom":sQuery(id+"F26.wireOp",EDGE,"E53.3.0")}),-1.0]])]});
            var Q4;
            Q4=makeQuery(id+"F26.imprint","IMPRINT",FACE,{"disambiguationData":[TD([[makeQuery(id+"F26.imprint","IMPRINT",EDGE,{"derivedFrom":sQuery(id+"F26.wireOp",EDGE,"E53.4.0")}),-1.0]])]});
            var Q5;
            Q5=makeQuery(id+"F26.imprint","IMPRINT",FACE,{"disambiguationData":[TD([[makeQuery(id+"F26.imprint","IMPRINT",EDGE,{"derivedFrom":sQuery(id+"F26.wireOp",EDGE,"E53.5.0")}),-1.0]])]});
            var Q6;
            Q6=makeQuery(id+"F26.imprint","IMPRINT",FACE,{"disambiguationData":[TD([[makeQuery(id+"F26.imprint","IMPRINT",EDGE,{"derivedFrom":sQuery(id+"F26.wireOp",EDGE,"E53.6.0")}),-1.0]])]});
            var Q7;
            Q7=makeQuery(id+"F26.imprint","IMPRINT",FACE,{"disambiguationData":[TD([[makeQuery(id+"F26.imprint","IMPRINT",EDGE,{"derivedFrom":sQuery(id+"F26.wireOp",EDGE,"E53.7.0")}),-1.0]])]});
            extrude(context, id + "F27", {"entities" : qUnion([Q0, Q1, Q2, Q3, Q4, Q5, Q6, Q7]), "operationType" : NewBodyOperationType.REMOVE, "oppositeDirection" : true, "depth" : 25.4 * mm, "offsetDistance" : 25.4 * mm});
        }
        {
            var Q0;
            Q0=makeQuery(id+"F1.opExtrude","CAP_FACE",FACE,{"disambiguationData":[OSD([sQuery(id+"F0.wireOp",EDGE,"E0.bottom"),sQuery(id+"F0.wireOp",EDGE,"E0.top"),sQuery(id+"F0.wireOp",EDGE,"E0.left"),sQuery(id+"F0.wireOp",EDGE,"E0.right")])],"isStart":false});
            var sketch = newSketch(context, id + "F28", { "sketchPlane" : qUnion([Q0])});
            skArc(sketch, "E54", {"start": v(21.83, 5.52) * mm, "mid": v(31, 14.29) * mm, "end": v(21.83, 23.06) * mm});
            skArc(sketch, "E55", {"start": v(21.83, 5.52) * mm, "mid": v(26.47, 14.29) * mm, "end": v(21.83, 23.06) * mm});
            skPoint(sketch, "E56", {"position": v(18.26, 14.29) * mm});
            skSolve(sketch);
        }
        {
            var Q0;
            Q0=makeQuery(id+"F28.imprint","IMPRINT",FACE,{"disambiguationData":[TD([[makeQuery(id+"F28.imprint","IMPRINT",EDGE,{"derivedFrom":sQuery(id+"F28.wireOp",EDGE,"E54")}),1.0]])]});
            extrude(context, id + "F29", {"entities" : qUnion([Q0]), "operationType" : NewBodyOperationType.REMOVE, "oppositeDirection" : true, "depth" : 25.4 * mm, "offsetDistance" : 25.4 * mm});
        }
        {
            var Q0;
            Q0=makeQuery(id+"F1.opExtrude","CAP_FACE",FACE,{"disambiguationData":[OSD([sQuery(id+"F0.wireOp",EDGE,"E0.bottom"),sQuery(id+"F0.wireOp",EDGE,"E0.top"),sQuery(id+"F0.wireOp",EDGE,"E0.left"),sQuery(id+"F0.wireOp",EDGE,"E0.right")])],"isStart":false});
            var sketch = newSketch(context, id + "F30", { "sketchPlane" : qUnion([Q0])});
            skArc(sketch, "E57", {"start": v(32.58, -7.79) * mm, "mid": v(24.8, 3.73) * mm, "end": v(11.57, -0.54) * mm});
            skArc(sketch, "E58", {"start": v(31.57, -7.79) * mm, "mid": v(24.59, 2.73) * mm, "end": v(12.52, -0.96) * mm});
            skArc(sketch, "E59", {"start": v(29.87, -7.79) * mm, "mid": v(24.07, 1.12) * mm, "end": v(13.89, -1.95) * mm});
            skArc(sketch, "E60", {"start": v(28.86, -7.79) * mm, "mid": v(23.66, 0.2) * mm, "end": v(14.59, -2.71) * mm});
            skArc(sketch, "E61", {"start": v(27.16, -7.79) * mm, "mid": v(22.76, -1.3) * mm, "end": v(15.55, -4.37) * mm});
            skArc(sketch, "E62", {"start": v(26.15, -7.79) * mm, "mid": v(22, -2.15) * mm, "end": v(16.06, -5.84) * mm});
            skLineSegment(sketch, "E63.trimOffspring", {"start": v(26.15, -7.79) * mm, "end": v(27.16, -7.79) * mm});
            skLineSegment(sketch, "E64.trimOffspring", {"start": v(28.86, -7.79) * mm, "end": v(29.87, -7.79) * mm});
            skLineSegment(sketch, "E65.trimOffspring", {"start": v(31.57, -7.79) * mm, "end": v(32.58, -7.79) * mm});
            skArc(sketch, "E66", {"start": v(24.45, -7.79) * mm, "mid": v(22.2, -3.93) * mm, "end": v(18, -5.49) * mm});
            skArc(sketch, "E67", {"start": v(23.44, -7.79) * mm, "mid": v(22.12, -4.98) * mm, "end": v(19.1, -5.66) * mm});
            skLineSegment(sketch, "E68.trimOffspring", {"start": v(23.44, -7.79) * mm, "end": v(24.45, -7.79) * mm});
            skLineSegment(sketch, "E69.trimOffspring", {"start": v(26.14, -7.79) * mm, "end": v(26.15, -7.79) * mm});
            skArc(sketch, "E70", {"start": v(15.27, -7.04) * mm, "mid": v(8.76, -0.93) * mm, "end": v(3.32, -8) * mm});
            skArc(sketch, "E71", {"start": v(3.32, -8) * mm, "mid": v(0.86, -11.75) * mm, "end": v(4.24, -14.7) * mm});
            skArc(sketch, "E72", {"start": v(15.27, -7.04) * mm, "mid": v(19.56, -6.5) * mm, "end": v(21.9, -10.13) * mm});
            skArc(sketch, "E73", {"start": v(21.9, -10.13) * mm, "mid": v(24.57, -12.41) * mm, "end": v(21.9, -14.7) * mm});
            skLineSegment(sketch, "E74", {"start": v(21.9, -14.7) * mm, "end": v(4.24, -14.7) * mm});
            skArc(sketch, "E75.trimOffspring", {"start": v(16, -6.08) * mm, "mid": v(14.56, -2.69) * mm, "end": v(11.57, -0.54) * mm});
            skArc(sketch, "E76.trimOffspring", {"start": v(19.1, -5.66) * mm, "mid": v(17.51, -5.5) * mm, "end": v(15.97, -5.88) * mm});
            skSolve(sketch);
        }
        {
            var Q0;
            Q0 = qSketchRegion(id + "F30", true);
            extrude(context, id + "F31", {"entities" : qUnion([Q0]), "operationType" : NewBodyOperationType.REMOVE, "oppositeDirection" : true, "depth" : 25.4 * mm, "offsetDistance" : 25.4 * mm});
        }
        {
            var Q0;
            Q0=makeQuery(id+"F1.opExtrude","CAP_FACE",FACE,{"disambiguationData":[OSD([sQuery(id+"F0.wireOp",EDGE,"E0.bottom"),sQuery(id+"F0.wireOp",EDGE,"E0.top"),sQuery(id+"F0.wireOp",EDGE,"E0.left"),sQuery(id+"F0.wireOp",EDGE,"E0.right")])],"isStart":false});
            var sketch = newSketch(context, id + "F32", { "sketchPlane" : qUnion([Q0])});
            skArc(sketch, "E77", {"start": v(1.94, -7.67) * mm, "mid": v(-8.25, 2.24) * mm, "end": v(-18.43, -7.67) * mm});
            skArc(sketch, "E78", {"start": v(1.94, -7.67) * mm, "mid": v(-1.4, -5.76) * mm, "end": v(-5.07, -6.94) * mm});
            skArc(sketch, "E79", {"start": v(-5.07, -6.94) * mm, "mid": v(-8.25, -5.73) * mm, "end": v(-11.42, -6.94) * mm});
            skArc(sketch, "E80", {"start": v(-11.42, -6.94) * mm, "mid": v(-15.09, -5.76) * mm, "end": v(-18.43, -7.67) * mm});
            skLineSegment(sketch, "E81.bottom", {"start": v(-7.61, -6.11) * mm, "end": v(-8.88, -6.11) * mm});
            skLineSegment(sketch, "E81.top", {"start": v(-8.88, -16.04) * mm, "end": v(-10.06, -16.04) * mm});
            skLineSegment(sketch, "E81.left", {"start": v(-7.61, -6.11) * mm, "end": v(-7.61, -14.26) * mm});
            skLineSegment(sketch, "E81.right", {"start": v(-8.88, -6.11) * mm, "end": v(-8.88, -14.26) * mm});
            skLineSegment(sketch, "E82.bottom", {"start": v(-5.58, -14.77) * mm, "end": v(-7.1, -14.77) * mm});
            skLineSegment(sketch, "E82.top", {"start": v(-5.58, -16.04) * mm, "end": v(-7.1, -16.04) * mm});
            skLineSegment(sketch, "E82.left", {"start": v(-5.58, -14.77) * mm, "end": v(-5.58, -16.04) * mm});
            skLineSegment(sketch, "E82.right", {"start": v(-8.88, -14.77) * mm, "end": v(-8.88, -16.04) * mm});
            skArc(sketch, "E83.filletArc", {"start": v(-7.61, -14.26) * mm, "mid": v(-7.46, -14.62) * mm, "end": v(-7.1, -14.77) * mm});
            skPoint(sketch, "E84.visualSharp", {"position": v(-8.88, -16.04) * mm});
            skArc(sketch, "E84.filletArc", {"start": v(-8.88, -14.26) * mm, "mid": v(-8.36, -15.52) * mm, "end": v(-7.1, -16.04) * mm});
            skPoint(sketch, "E85", {"position": v(7.62, -10.82) * mm});
            skSolve(sketch);
        }
        {
            var Q0;
            Q0 = qSketchRegion(id + "F32", true);
            extrude(context, id + "F33", {"entities" : qUnion([Q0]), "operationType" : NewBodyOperationType.REMOVE, "oppositeDirection" : true, "depth" : 25.4 * mm, "offsetDistance" : 25.4 * mm});
        }
        {
            var Q0;
            Q0=makeQuery(id+"F1.opExtrude","CAP_FACE",FACE,{"disambiguationData":[OSD([sQuery(id+"F0.wireOp",EDGE,"E0.bottom"),sQuery(id+"F0.wireOp",EDGE,"E0.top"),sQuery(id+"F0.wireOp",EDGE,"E0.left"),sQuery(id+"F0.wireOp",EDGE,"E0.right")])],"isStart":false});
            var sketch = newSketch(context, id + "F34", { "sketchPlane" : qUnion([Q0])});
            skArc(sketch, "E86", {"start": v(-22.4, -13.41) * mm, "mid": v(-23.14, -13.66) * mm, "end": v(-23.8, -14.09) * mm});
            skLineSegment(sketch, "E87", {"start": v(-21.76, -16.52) * mm, "end": v(-21.76, -9.48) * mm, "construction": true});
            skLineSegment(sketch, "E88.left", {"start": v(-22.4, -9.5) * mm, "end": v(-22.4, -9.93) * mm});
            skLineSegment(sketch, "E88.right", {"start": v(-21.13, -9.5) * mm, "end": v(-21.13, -9.93) * mm});
            skLineSegment(sketch, "E89.bottom", {"start": v(-24.2, -7.7) * mm, "end": v(-23.3, -6.8) * mm});
            skLineSegment(sketch, "E89.left", {"start": v(-24.2, -7.7) * mm, "end": v(-22.4, -9.5) * mm});
            skLineSegment(sketch, "E89.right", {"start": v(-23.3, -6.8) * mm, "end": v(-21.76, -8.34) * mm});
            skLineSegment(sketch, "E90.MirrorCS", {"start": v(-19.33, -7.7) * mm, "end": v(-20.23, -6.8) * mm});
            skLineSegment(sketch, "E91.MirrorCS", {"start": v(-20.23, -6.8) * mm, "end": v(-21.76, -8.34) * mm});
            skLineSegment(sketch, "E92.MirrorCS", {"start": v(-19.33, -7.7) * mm, "end": v(-21.13, -9.5) * mm});
            skLineSegment(sketch, "E93.bottom", {"start": v(-24.2, -9.93) * mm, "end": v(-23.3, -9.03) * mm});
            skLineSegment(sketch, "E93.left", {"start": v(-24.2, -9.93) * mm, "end": v(-22.4, -11.73) * mm});
            skLineSegment(sketch, "E93.right", {"start": v(-23.3, -9.03) * mm, "end": v(-22.4, -9.93) * mm});
            skLineSegment(sketch, "E94.MirrorCS", {"start": v(-19.33, -9.93) * mm, "end": v(-20.23, -9.03) * mm});
            skLineSegment(sketch, "E95.MirrorCS", {"start": v(-20.23, -9.03) * mm, "end": v(-21.13, -9.93) * mm});
            skLineSegment(sketch, "E96.MirrorCS", {"start": v(-19.33, -9.93) * mm, "end": v(-21.13, -11.73) * mm});
            skPoint(sketch, "E97.orphan", {"position": v(-21.5, -8.6) * mm});
            skPoint(sketch, "E98.orphan", {"position": v(-22.03, -8.6) * mm});
            skLineSegment(sketch, "E99.trimOffspring", {"start": v(-22.4, -11.73) * mm, "end": v(-22.4, -13.41) * mm});
            skLineSegment(sketch, "E100.trimOffspring", {"start": v(-21.13, -11.73) * mm, "end": v(-21.13, -13.41) * mm});
            skLineSegment(sketch, "E101.1.0", {"start": v(-30.18, -12.92) * mm, "end": v(-27.65, -12.64) * mm});
            skLineSegment(sketch, "E101.1.1", {"start": v(-25.4, -10.51) * mm, "end": v(-26.67, -10.66) * mm});
            skLineSegment(sketch, "E101.1.2", {"start": v(-28.4, -9.27) * mm, "end": v(-28.17, -11.42) * mm});
            skLineSegment(sketch, "E101.1.3", {"start": v(-28.58, -13.05) * mm, "end": v(-27.31, -12.91) * mm});
            skLineSegment(sketch, "E101.1.4", {"start": v(-30.32, -11.66) * mm, "end": v(-28.17, -11.42) * mm});
            skPoint(sketch, "E101.1.5", {"position": v(-27.8, -11.38) * mm});
            skLineSegment(sketch, "E101.1.6", {"start": v(-25.12, -13.04) * mm, "end": v(-23.8, -14.09) * mm});
            skLineSegment(sketch, "E101.1.7", {"start": v(-28.43, -14.31) * mm, "end": v(-25.91, -14.03) * mm});
            skLineSegment(sketch, "E101.1.8", {"start": v(-27.15, -9.12) * mm, "end": v(-28.4, -9.27) * mm});
            skLineSegment(sketch, "E101.1.9", {"start": v(-25.4, -10.51) * mm, "end": v(-25.12, -13.04) * mm});
            skLineSegment(sketch, "E101.1.10", {"start": v(-25.91, -14.03) * mm, "end": v(-24.6, -15.08) * mm});
            skPoint(sketch, "E101.1.11", {"position": v(-28.12, -11.79) * mm});
            skLineSegment(sketch, "E101.1.12", {"start": v(-27.15, -9.12) * mm, "end": v(-26.86, -11.65) * mm});
            skLineSegment(sketch, "E101.1.13", {"start": v(-28.43, -14.31) * mm, "end": v(-28.58, -13.05) * mm});
            skLineSegment(sketch, "E101.1.14", {"start": v(-26.67, -10.66) * mm, "end": v(-26.52, -11.92) * mm});
            skLineSegment(sketch, "E101.1.15", {"start": v(-30.18, -12.92) * mm, "end": v(-30.32, -11.66) * mm});
            skLineSegment(sketch, "E101.1.16", {"start": v(-27.65, -12.64) * mm, "end": v(-27.31, -12.91) * mm});
            skLineSegment(sketch, "E101.1.17", {"start": v(-26.86, -11.65) * mm, "end": v(-26.52, -11.92) * mm});
            skLineSegment(sketch, "E101.2.0", {"start": v(-29.82, -20.86) * mm, "end": v(-28.47, -18.7) * mm});
            skLineSegment(sketch, "E101.2.1", {"start": v(-28.73, -15.62) * mm, "end": v(-29.4, -16.7) * mm});
            skLineSegment(sketch, "E101.2.2", {"start": v(-31.58, -17.2) * mm, "end": v(-29.75, -18.35) * mm});
            skLineSegment(sketch, "E101.2.3", {"start": v(-28.73, -19.69) * mm, "end": v(-28.05, -18.61) * mm});
            skLineSegment(sketch, "E101.2.4", {"start": v(-30.9, -20.18) * mm, "end": v(-29.75, -18.35) * mm});
            skPoint(sketch, "E101.2.5", {"position": v(-29.55, -18.03) * mm});
            skLineSegment(sketch, "E101.2.6", {"start": v(-26.58, -16.97) * mm, "end": v(-24.94, -16.6) * mm});
            skLineSegment(sketch, "E101.2.7", {"start": v(-27.65, -20.36) * mm, "end": v(-26.3, -18.21) * mm});
            skLineSegment(sketch, "E101.2.8", {"start": v(-30.9, -16.12) * mm, "end": v(-31.58, -17.2) * mm});
            skLineSegment(sketch, "E101.2.9", {"start": v(-28.73, -15.62) * mm, "end": v(-26.58, -16.97) * mm});
            skLineSegment(sketch, "E101.2.10", {"start": v(-26.3, -18.21) * mm, "end": v(-24.66, -17.84) * mm});
            skPoint(sketch, "E101.2.11", {"position": v(-29.43, -18.54) * mm});
            skLineSegment(sketch, "E101.2.12", {"start": v(-30.9, -16.12) * mm, "end": v(-28.76, -17.47) * mm});
            skLineSegment(sketch, "E101.2.13", {"start": v(-27.65, -20.36) * mm, "end": v(-28.73, -19.69) * mm});
            skLineSegment(sketch, "E101.2.14", {"start": v(-29.4, -16.7) * mm, "end": v(-28.33, -17.37) * mm});
            skLineSegment(sketch, "E101.2.15", {"start": v(-29.82, -20.86) * mm, "end": v(-30.9, -20.18) * mm});
            skLineSegment(sketch, "E101.2.16", {"start": v(-28.47, -18.7) * mm, "end": v(-28.05, -18.61) * mm});
            skLineSegment(sketch, "E101.2.17", {"start": v(-28.76, -17.47) * mm, "end": v(-28.33, -17.37) * mm});
            skLineSegment(sketch, "E101.3.0", {"start": v(-23.4, -25.53) * mm, "end": v(-24.24, -23.13) * mm});
            skLineSegment(sketch, "E101.3.1", {"start": v(-26.82, -21.41) * mm, "end": v(-26.4, -22.6) * mm});
            skLineSegment(sketch, "E101.3.2", {"start": v(-27.36, -24.62) * mm, "end": v(-25.32, -23.9) * mm});
            skLineSegment(sketch, "E101.3.3", {"start": v(-23.63, -23.94) * mm, "end": v(-24.05, -22.74) * mm});
            skLineSegment(sketch, "E101.3.4", {"start": v(-24.6, -25.95) * mm, "end": v(-25.32, -23.9) * mm});
            skPoint(sketch, "E101.3.5", {"position": v(-25.44, -23.55) * mm});
            skLineSegment(sketch, "E101.3.6", {"start": v(-24.42, -20.57) * mm, "end": v(-23.69, -19.05) * mm});
            skLineSegment(sketch, "E101.3.7", {"start": v(-22.43, -23.52) * mm, "end": v(-23.27, -21.12) * mm});
            skLineSegment(sketch, "E101.3.8", {"start": v(-27.78, -23.42) * mm, "end": v(-27.36, -24.62) * mm});
            skLineSegment(sketch, "E101.3.9", {"start": v(-26.82, -21.41) * mm, "end": v(-24.42, -20.57) * mm});
            skLineSegment(sketch, "E101.3.10", {"start": v(-23.27, -21.12) * mm, "end": v(-22.54, -19.6) * mm});
            skPoint(sketch, "E101.3.11", {"position": v(-24.97, -23.78) * mm});
            skLineSegment(sketch, "E101.3.12", {"start": v(-27.78, -23.42) * mm, "end": v(-25.38, -22.58) * mm});
            skLineSegment(sketch, "E101.3.13", {"start": v(-22.43, -23.52) * mm, "end": v(-23.63, -23.94) * mm});
            skLineSegment(sketch, "E101.3.14", {"start": v(-26.4, -22.6) * mm, "end": v(-25.2, -22.19) * mm});
            skLineSegment(sketch, "E101.3.15", {"start": v(-23.4, -25.53) * mm, "end": v(-24.6, -25.95) * mm});
            skLineSegment(sketch, "E101.3.16", {"start": v(-24.24, -23.13) * mm, "end": v(-24.05, -22.74) * mm});
            skLineSegment(sketch, "E101.3.17", {"start": v(-25.38, -22.58) * mm, "end": v(-25.2, -22.19) * mm});
            skLineSegment(sketch, "E101.4.0", {"start": v(-15.75, -23.42) * mm, "end": v(-18.14, -22.58) * mm});
            skLineSegment(sketch, "E101.4.1", {"start": v(-21.1, -23.52) * mm, "end": v(-19.9, -23.94) * mm});
            skLineSegment(sketch, "E101.4.2", {"start": v(-18.93, -25.95) * mm, "end": v(-18.21, -23.9) * mm});
            skLineSegment(sketch, "E101.4.3", {"start": v(-17.13, -22.6) * mm, "end": v(-18.33, -22.19) * mm});
            skLineSegment(sketch, "E101.4.4", {"start": v(-16.17, -24.62) * mm, "end": v(-18.21, -23.9) * mm});
            skPoint(sketch, "E101.4.5", {"position": v(-18.56, -23.78) * mm});
            skLineSegment(sketch, "E101.4.6", {"start": v(-20.25, -21.12) * mm, "end": v(-20.99, -19.6) * mm});
            skLineSegment(sketch, "E101.4.7", {"start": v(-16.71, -21.41) * mm, "end": v(-19.11, -20.57) * mm});
            skLineSegment(sketch, "E101.4.8", {"start": v(-20.13, -25.53) * mm, "end": v(-18.93, -25.95) * mm});
            skLineSegment(sketch, "E101.4.9", {"start": v(-21.1, -23.52) * mm, "end": v(-20.25, -21.12) * mm});
            skLineSegment(sketch, "E101.4.10", {"start": v(-19.11, -20.57) * mm, "end": v(-19.84, -19.05) * mm});
            skPoint(sketch, "E101.4.11", {"position": v(-18.09, -23.55) * mm});
            skLineSegment(sketch, "E101.4.12", {"start": v(-20.13, -25.53) * mm, "end": v(-19.29, -23.13) * mm});
            skLineSegment(sketch, "E101.4.13", {"start": v(-16.71, -21.41) * mm, "end": v(-17.13, -22.6) * mm});
            skLineSegment(sketch, "E101.4.14", {"start": v(-19.9, -23.94) * mm, "end": v(-19.48, -22.74) * mm});
            skLineSegment(sketch, "E101.4.15", {"start": v(-15.75, -23.42) * mm, "end": v(-16.17, -24.62) * mm});
            skLineSegment(sketch, "E101.4.16", {"start": v(-18.14, -22.58) * mm, "end": v(-18.33, -22.19) * mm});
            skLineSegment(sketch, "E101.4.17", {"start": v(-19.29, -23.13) * mm, "end": v(-19.48, -22.74) * mm});
            skLineSegment(sketch, "E101.5.0", {"start": v(-12.62, -16.12) * mm, "end": v(-14.77, -17.47) * mm});
            skLineSegment(sketch, "E101.5.1", {"start": v(-15.88, -20.36) * mm, "end": v(-14.8, -19.69) * mm});
            skLineSegment(sketch, "E101.5.2", {"start": v(-12.63, -20.18) * mm, "end": v(-13.78, -18.35) * mm});
            skLineSegment(sketch, "E101.5.3", {"start": v(-14.12, -16.7) * mm, "end": v(-15.2, -17.37) * mm});
            skLineSegment(sketch, "E101.5.4", {"start": v(-11.95, -17.2) * mm, "end": v(-13.78, -18.35) * mm});
            skPoint(sketch, "E101.5.5", {"position": v(-14.1, -18.54) * mm});
            skLineSegment(sketch, "E101.5.6", {"start": v(-17.23, -18.21) * mm, "end": v(-18.87, -17.84) * mm});
            skLineSegment(sketch, "E101.5.7", {"start": v(-14.8, -15.62) * mm, "end": v(-16.95, -16.97) * mm});
            skLineSegment(sketch, "E101.5.8", {"start": v(-13.7, -20.86) * mm, "end": v(-12.63, -20.18) * mm});
            skLineSegment(sketch, "E101.5.9", {"start": v(-15.88, -20.36) * mm, "end": v(-17.23, -18.21) * mm});
            skLineSegment(sketch, "E101.5.10", {"start": v(-16.95, -16.97) * mm, "end": v(-18.59, -16.6) * mm});
            skPoint(sketch, "E101.5.11", {"position": v(-13.98, -18.03) * mm});
            skLineSegment(sketch, "E101.5.12", {"start": v(-13.7, -20.86) * mm, "end": v(-15.05, -18.7) * mm});
            skLineSegment(sketch, "E101.5.13", {"start": v(-14.8, -15.62) * mm, "end": v(-14.12, -16.7) * mm});
            skLineSegment(sketch, "E101.5.14", {"start": v(-14.8, -19.69) * mm, "end": v(-15.48, -18.61) * mm});
            skLineSegment(sketch, "E101.5.15", {"start": v(-12.62, -16.12) * mm, "end": v(-11.95, -17.2) * mm});
            skLineSegment(sketch, "E101.5.16", {"start": v(-14.77, -17.47) * mm, "end": v(-15.2, -17.37) * mm});
            skLineSegment(sketch, "E101.5.17", {"start": v(-15.05, -18.7) * mm, "end": v(-15.48, -18.61) * mm});
            skLineSegment(sketch, "E101.6.0", {"start": v(-16.38, -9.12) * mm, "end": v(-16.67, -11.65) * mm});
            skLineSegment(sketch, "E101.6.1", {"start": v(-15.1, -14.31) * mm, "end": v(-14.95, -13.05) * mm});
            skLineSegment(sketch, "E101.6.2", {"start": v(-13.2, -11.66) * mm, "end": v(-15.36, -11.42) * mm});
            skLineSegment(sketch, "E101.6.3", {"start": v(-16.86, -10.66) * mm, "end": v(-17, -11.92) * mm});
            skLineSegment(sketch, "E101.6.4", {"start": v(-15.12, -9.27) * mm, "end": v(-15.36, -11.42) * mm});
            skPoint(sketch, "E101.6.5", {"position": v(-15.4, -11.79) * mm});
            skLineSegment(sketch, "E101.6.6", {"start": v(-17.62, -14.03) * mm, "end": v(-18.94, -15.08) * mm});
            skLineSegment(sketch, "E101.6.7", {"start": v(-18.12, -10.51) * mm, "end": v(-18.4, -13.04) * mm});
            skLineSegment(sketch, "E101.6.8", {"start": v(-13.35, -12.92) * mm, "end": v(-13.2, -11.66) * mm});
            skLineSegment(sketch, "E101.6.9", {"start": v(-15.1, -14.31) * mm, "end": v(-17.62, -14.03) * mm});
            skLineSegment(sketch, "E101.6.10", {"start": v(-18.4, -13.04) * mm, "end": v(-19.73, -14.09) * mm});
            skPoint(sketch, "E101.6.11", {"position": v(-15.73, -11.38) * mm});
            skLineSegment(sketch, "E101.6.12", {"start": v(-13.35, -12.92) * mm, "end": v(-15.87, -12.64) * mm});
            skLineSegment(sketch, "E101.6.13", {"start": v(-18.12, -10.51) * mm, "end": v(-16.86, -10.66) * mm});
            skLineSegment(sketch, "E101.6.14", {"start": v(-14.95, -13.05) * mm, "end": v(-16.21, -12.91) * mm});
            skLineSegment(sketch, "E101.6.15", {"start": v(-16.38, -9.12) * mm, "end": v(-15.12, -9.27) * mm});
            skLineSegment(sketch, "E101.6.16", {"start": v(-16.67, -11.65) * mm, "end": v(-17, -11.92) * mm});
            skLineSegment(sketch, "E101.6.17", {"start": v(-15.87, -12.64) * mm, "end": v(-16.21, -12.91) * mm});
            skArc(sketch, "E102.trimOffspring", {"start": v(-24.6, -15.08) * mm, "mid": v(-24.86, -15.82) * mm, "end": v(-24.94, -16.6) * mm});
            skArc(sketch, "E103.trimOffspring", {"start": v(-24.66, -17.84) * mm, "mid": v(-24.25, -18.5) * mm, "end": v(-23.69, -19.05) * mm});
            skArc(sketch, "E104.trimOffspring", {"start": v(-22.54, -19.6) * mm, "mid": v(-21.76, -19.7) * mm, "end": v(-20.99, -19.6) * mm});
            skArc(sketch, "E105.trimOffspring", {"start": v(-19.84, -19.05) * mm, "mid": v(-19.28, -18.5) * mm, "end": v(-18.87, -17.84) * mm});
            skArc(sketch, "E106.trimOffspring", {"start": v(-18.59, -16.6) * mm, "mid": v(-18.67, -15.82) * mm, "end": v(-18.94, -15.08) * mm});
            skArc(sketch, "E107.trimOffspring", {"start": v(-19.73, -14.09) * mm, "mid": v(-20.39, -13.66) * mm, "end": v(-21.13, -13.41) * mm});
            skSolve(sketch);
        }
        {
            var Q0;
            Q0=makeQuery(id+"F1.opExtrude","CAP_FACE",FACE,{"disambiguationData":[OSD([sQuery(id+"F0.wireOp",EDGE,"E0.bottom"),sQuery(id+"F0.wireOp",EDGE,"E0.top"),sQuery(id+"F0.wireOp",EDGE,"E0.left"),sQuery(id+"F0.wireOp",EDGE,"E0.right")])],"isStart":false});
            var sketch = newSketch(context, id + "F35", { "sketchPlane" : qUnion([Q0])});
            skLineSegment(sketch, "E108.bottom", {"start": v(5.56, -24.54) * mm, "end": v(30.96, -24.54) * mm});
            skLineSegment(sketch, "E108.top", {"start": v(5.56, -25.8) * mm, "end": v(30.96, -25.8) * mm});
            skLineSegment(sketch, "E108.left", {"start": v(5.56, -24.54) * mm, "end": v(5.56, -25.8) * mm});
            skLineSegment(sketch, "E108.right", {"start": v(30.96, -24.54) * mm, "end": v(30.96, -25.8) * mm});
            skArc(sketch, "E109", {"start": v(9.5, -18.24) * mm, "mid": v(9.13, -19.1) * mm, "end": v(9.07, -20.04) * mm});
            skCircle(sketch, "E110", {"center": v(11.91, -19.77) * mm, "radius": 2.54 * mm});
            skCircle(sketch, "E111.cCircle", {"center": v(11.89, -22.87) * mm, "radius": 0.6 * mm, "construction": true});
            skLineSegment(sketch, "E111.0", {"start": v(10.85, -22.27) * mm, "end": v(12.93, -22.27) * mm});
            skLineSegment(sketch, "E111.1", {"start": v(12.8, -22.49) * mm, "end": v(11.89, -24.08) * mm});
            skLineSegment(sketch, "E111.2", {"start": v(11.89, -24.08) * mm, "end": v(10.96, -22.47) * mm});
            skPoint(sketch, "E111.0.midPoint", {"position": v(11.89, -22.27) * mm});
            skLineSegment(sketch, "E112.1.0", {"start": v(14.6, -20.76) * mm, "end": v(15.26, -22.47) * mm});
            skLineSegment(sketch, "E112.1.1", {"start": v(15.26, -22.47) * mm, "end": v(13.42, -22.2) * mm});
            skPoint(sketch, "E112.1.2", {"position": v(13.85, -21.35) * mm});
            skCircle(sketch, "E112.1.4", {"center": v(14.32, -21.72) * mm, "radius": 0.6 * mm, "construction": true});
            skLineSegment(sketch, "E112.2.0", {"start": v(14.36, -18.3) * mm, "end": v(16.11, -18.84) * mm});
            skLineSegment(sketch, "E112.2.1", {"start": v(16.11, -18.84) * mm, "end": v(14.75, -20.1) * mm});
            skPoint(sketch, "E112.2.2", {"position": v(14.35, -19.24) * mm});
            skCircle(sketch, "E112.2.4", {"center": v(14.94, -19.1) * mm, "radius": 0.6 * mm, "construction": true});
            skLineSegment(sketch, "E112.3.0", {"start": v(12.28, -16.94) * mm, "end": v(13.8, -15.9) * mm});
            skLineSegment(sketch, "E112.3.1", {"start": v(13.8, -15.9) * mm, "end": v(13.94, -17.76) * mm});
            skPoint(sketch, "E112.3.2", {"position": v(13.02, -17.53) * mm});
            skCircle(sketch, "E112.3.4", {"center": v(13.28, -17) * mm, "radius": 0.6 * mm, "construction": true});
            skLineSegment(sketch, "E112.4.0", {"start": v(9.93, -17.72) * mm, "end": v(10.07, -15.89) * mm});
            skLineSegment(sketch, "E112.4.1", {"start": v(10.07, -15.89) * mm, "end": v(11.6, -16.93) * mm});
            skPoint(sketch, "E112.4.2", {"position": v(10.85, -17.51) * mm});
            skCircle(sketch, "E112.4.4", {"center": v(10.59, -16.97) * mm, "radius": 0.6 * mm, "construction": true});
            skLineSegment(sketch, "E112.5.0", {"start": v(9.07, -20.04) * mm, "end": v(7.72, -18.8) * mm});
            skLineSegment(sketch, "E112.5.1", {"start": v(7.72, -18.8) * mm, "end": v(9.5, -18.24) * mm});
            skPoint(sketch, "E112.5.2", {"position": v(9.48, -19.2) * mm});
            skCircle(sketch, "E112.5.4", {"center": v(8.9, -19.06) * mm, "radius": 0.6 * mm, "construction": true});
            skLineSegment(sketch, "E112.6.0", {"start": v(10.35, -22.16) * mm, "end": v(8.53, -22.44) * mm});
            skLineSegment(sketch, "E112.6.1", {"start": v(8.53, -22.44) * mm, "end": v(9.21, -20.7) * mm});
            skPoint(sketch, "E112.6.2", {"position": v(9.95, -21.31) * mm});
            skCircle(sketch, "E112.6.4", {"center": v(9.48, -21.69) * mm, "radius": 0.6 * mm, "construction": true});
            skArc(sketch, "E113.trimOffspring", {"start": v(11.6, -16.93) * mm, "mid": v(10.7, -17.19) * mm, "end": v(9.93, -17.72) * mm});
            skArc(sketch, "E114.trimOffspring", {"start": v(13.94, -17.76) * mm, "mid": v(13.18, -17.21) * mm, "end": v(12.28, -16.94) * mm});
            skArc(sketch, "E115.trimOffspring", {"start": v(14.75, -20.1) * mm, "mid": v(14.7, -19.17) * mm, "end": v(14.36, -18.3) * mm});
            skArc(sketch, "E116.trimOffspring", {"start": v(9.21, -20.7) * mm, "mid": v(9.66, -21.53) * mm, "end": v(10.35, -22.16) * mm});
            skArc(sketch, "E117.trimOffspring", {"start": v(10.96, -22.47) * mm, "mid": v(11.88, -22.63) * mm, "end": v(12.8, -22.49) * mm});
            skArc(sketch, "E118.trimOffspring", {"start": v(13.42, -22.2) * mm, "mid": v(14.13, -21.58) * mm, "end": v(14.6, -20.76) * mm});
            skArc(sketch, "E119", {"start": v(22.2, -20.98) * mm, "mid": v(21.88, -21.66) * mm, "end": v(21.76, -22.41) * mm});
            skArc(sketch, "E120", {"start": v(27.15, -22.41) * mm, "mid": v(24.61, -19.96) * mm, "end": v(22.07, -22.41) * mm});
            skLineSegment(sketch, "E121.2.0", {"start": v(27.06, -21.03) * mm, "end": v(28.81, -21.57) * mm});
            skLineSegment(sketch, "E121.2.1", {"start": v(28.81, -21.57) * mm, "end": v(27.9, -22.41) * mm});
            skLineSegment(sketch, "E121.3.0", {"start": v(24.98, -19.67) * mm, "end": v(26.5, -18.64) * mm});
            skLineSegment(sketch, "E121.3.1", {"start": v(26.5, -18.64) * mm, "end": v(26.64, -20.5) * mm});
            skLineSegment(sketch, "E121.4.0", {"start": v(22.63, -20.45) * mm, "end": v(22.77, -18.62) * mm});
            skLineSegment(sketch, "E121.4.1", {"start": v(22.77, -18.62) * mm, "end": v(24.3, -19.66) * mm});
            skLineSegment(sketch, "E121.5.0", {"start": v(21.38, -22.41) * mm, "end": v(20.42, -21.52) * mm});
            skLineSegment(sketch, "E121.5.1", {"start": v(20.42, -21.52) * mm, "end": v(22.2, -20.98) * mm});
            skArc(sketch, "E122.trimOffspring", {"start": v(24.3, -19.66) * mm, "mid": v(23.4, -19.92) * mm, "end": v(22.63, -20.45) * mm});
            skArc(sketch, "E123.trimOffspring", {"start": v(26.64, -20.5) * mm, "mid": v(25.88, -19.94) * mm, "end": v(24.98, -19.67) * mm});
            skArc(sketch, "E124.trimOffspring", {"start": v(27.47, -22.41) * mm, "mid": v(27.35, -21.7) * mm, "end": v(27.06, -21.03) * mm});
            skLineSegment(sketch, "E125.bottom", {"start": v(21.38, -22.41) * mm, "end": v(21.76, -22.41) * mm});
            skLineSegment(sketch, "E126.trimOffspring", {"start": v(22.07, -22.41) * mm, "end": v(27.15, -22.41) * mm});
            skLineSegment(sketch, "E127", {"start": v(27.47, -22.41) * mm, "end": v(27.9, -22.41) * mm});
            skSolve(sketch);
        }
        {
            var Q0;
            {var subQ0=sQuery(id+"F35.wireOp",EDGE,"E111.0");var subQ1=sQuery(id+"F35.wireOp",EDGE,"E110");var subQ2=makeQuery(id+"F35.imprint","INTERSECT",VERTEX,{"disambiguationData":[OD(0.0)],"derivedFrom":[subQ1,subQ0]});Q0=makeQuery(id+"F35.imprint","IMPRINT",FACE,{"disambiguationData":[TD([[makeQuery(id+"F35.imprint","IMPRINT",EDGE,{"disambiguationData":[TD([[subQ2,1.0]])],"derivedFrom":subQ1}),1.0]])]});}
            var Q1;
            Q1=makeQuery(id+"F35.imprint","IMPRINT",FACE,{"disambiguationData":[TD([[makeQuery(id+"F35.imprint","IMPRINT",EDGE,{"derivedFrom":sQuery(id+"F35.wireOp",EDGE,"E121.4.0")}),-1.0]])]});
            var Q2;
            {var subQ0=sQuery(id+"F35.wireOp",EDGE,"E119");Q2=makeQuery(id+"F35.imprint","IMPRINT",FACE,{"disambiguationData":[TD([[makeQuery(id+"F35.imprint","IMPRINT",EDGE,{"derivedFrom":subQ0}),-1.0]])]});}
            var Q3;
            {var subQ0=sQuery(id+"F35.wireOp",EDGE,"E120");Q3=makeQuery(id+"F35.imprint","IMPRINT",FACE,{"disambiguationData":[TD([[makeQuery(id+"F35.imprint","IMPRINT",EDGE,{"derivedFrom":subQ0}),1.0]])]});}
            var Q4;
            Q4=makeQuery(id+"F35.imprint","IMPRINT",FACE,{"disambiguationData":[TD([[makeQuery(id+"F35.imprint","IMPRINT",EDGE,{"derivedFrom":sQuery(id+"F35.wireOp",EDGE,"E121.3.0")}),-1.0]])]});
            var Q5;
            Q5=makeQuery(id+"F35.imprint","IMPRINT",FACE,{"disambiguationData":[TD([[makeQuery(id+"F35.imprint","IMPRINT",EDGE,{"derivedFrom":sQuery(id+"F35.wireOp",EDGE,"E108.bottom")}),-1.0]])]});
            var Q6;
            Q6=makeQuery(id+"F35.imprint","IMPRINT",FACE,{"disambiguationData":[TD([[makeQuery(id+"F35.imprint","IMPRINT",EDGE,{"derivedFrom":sQuery(id+"F35.wireOp",EDGE,"E109")}),-1.0]])]});
            var Q7;
            Q7=makeQuery(id+"F35.imprint","IMPRINT",FACE,{"disambiguationData":[TD([[makeQuery(id+"F35.imprint","IMPRINT",EDGE,{"derivedFrom":sQuery(id+"F35.wireOp",EDGE,"E112.2.0")}),-1.0]])]});
            var Q8;
            {var subQ0=sQuery(id+"F35.wireOp",EDGE,"E121.2.0");Q8=makeQuery(id+"F35.imprint","IMPRINT",FACE,{"disambiguationData":[TD([[makeQuery(id+"F35.imprint","IMPRINT",EDGE,{"derivedFrom":subQ0}),-1.0]])]});}
            var Q9;
            Q9=makeQuery(id+"F35.imprint","IMPRINT",FACE,{"disambiguationData":[TD([[makeQuery(id+"F35.imprint","IMPRINT",EDGE,{"derivedFrom":sQuery(id+"F35.wireOp",EDGE,"E112.6.0")}),-1.0]])]});
            var Q10;
            Q10=makeQuery(id+"F35.imprint","IMPRINT",FACE,{"disambiguationData":[TD([[makeQuery(id+"F35.imprint","IMPRINT",EDGE,{"derivedFrom":sQuery(id+"F35.wireOp",EDGE,"E112.1.0")}),-1.0]])]});
            var Q11;
            Q11=makeQuery(id+"F35.imprint","IMPRINT",FACE,{"disambiguationData":[TD([[makeQuery(id+"F35.imprint","IMPRINT",EDGE,{"derivedFrom":sQuery(id+"F35.wireOp",EDGE,"E112.4.0")}),-1.0]])]});
            var Q12;
            Q12=makeQuery(id+"F35.imprint","IMPRINT",FACE,{"disambiguationData":[TD([[makeQuery(id+"F35.imprint","IMPRINT",EDGE,{"derivedFrom":sQuery(id+"F35.wireOp",EDGE,"E111.1")}),-1.0]])]});
            var Q13;
            Q13=makeQuery(id+"F35.imprint","IMPRINT",FACE,{"disambiguationData":[TD([[makeQuery(id+"F35.imprint","IMPRINT",EDGE,{"derivedFrom":sQuery(id+"F35.wireOp",EDGE,"E112.3.0")}),-1.0]])]});
            var Q14;
            {var subQ0=sQuery(id+"F35.wireOp",EDGE,"E111.0");var subQ1=sQuery(id+"F35.wireOp",EDGE,"E110");var subQ2=makeQuery(id+"F35.imprint","INTERSECT",VERTEX,{"disambiguationData":[OD(0.0)],"derivedFrom":[subQ1,subQ0]});Q14=makeQuery(id+"F35.imprint","IMPRINT",FACE,{"disambiguationData":[TD([[makeQuery(id+"F35.imprint","IMPRINT",EDGE,{"disambiguationData":[TD([[subQ2,-1.0]])],"derivedFrom":subQ1}),1.0]])]});}
            extrude(context, id + "F36", {"entities" : qUnion([Q0, Q1, Q2, Q3, Q4, Q5, Q6, Q7, Q8, Q9, Q10, Q11, Q12, Q13, Q14]), "operationType" : NewBodyOperationType.REMOVE, "oppositeDirection" : true, "depth" : 25.4 * mm, "offsetDistance" : 25.4 * mm});
        }
        {
            var Q0;
            Q0=makeQuery(id+"F1.opExtrude","CAP_FACE",FACE,{"disambiguationData":[OSD([sQuery(id+"F0.wireOp",EDGE,"E0.bottom"),sQuery(id+"F0.wireOp",EDGE,"E0.top"),sQuery(id+"F0.wireOp",EDGE,"E0.left"),sQuery(id+"F0.wireOp",EDGE,"E0.right")])],"isStart":false});
            var sketch = newSketch(context, id + "F37", { "sketchPlane" : qUnion([Q0])});
            skFitSpline(sketch, "E128", {"points": [v(-10.14, -18.7) * mm, v(-5.75, -18.25) * mm, v(-2.54, -18.05) * mm, v(-1.49, -16.8) * mm, v(-1.82, -15.76) * mm, v(-3.2, -15.43) * mm], "startDerivative": vector(9.44, 8.6) * mm, "endDerivative": vector(-11.17, 0.67) * mm});
            skFitSpline(sketch, "E129.0", {"points": [v(-9.45, -19.46) * mm, v(-9.42, -19.43) * mm, v(-9.34, -19.37) * mm, v(-9.12, -19.27) * mm, v(-8.8, -19.2) * mm, v(-8.27, -19.13) * mm, v(-7.47, -19.13) * mm, v(-6.4, -19.2) * mm, v(-5.35, -19.3) * mm, v(-4.35, -19.37) * mm, v(-3.56, -19.35) * mm, v(-2.93, -19.25) * mm, v(-2.47, -19.13) * mm, v(-2.01, -18.94) * mm, v(-1.6, -18.69) * mm, v(-1.24, -18.38) * mm, v(-0.93, -18.02) * mm, v(-0.68, -17.61) * mm, v(-0.5, -17.16) * mm, v(-0.44, -16.66) * mm, v(-0.47, -16.18) * mm, v(-0.6, -15.73) * mm, v(-0.8, -15.37) * mm, v(-1.01, -15.12) * mm, v(-1.2, -14.94) * mm, v(-1.41, -14.8) * mm, v(-1.7, -14.65) * mm, v(-2.04, -14.54) * mm, v(-2.42, -14.47) * mm, v(-2.78, -14.44) * mm, v(-3.02, -14.42) * mm, v(-3.13, -14.42) * mm]});
            skLineSegment(sketch, "E130", {"start": v(-3.13, -14.42) * mm, "end": v(-3.2, -15.43) * mm});
            skFitSpline(sketch, "E131", {"points": [v(-9.35, -21.39) * mm, v(-4.37, -20.93) * mm, v(1.33, -21.39) * mm, v(4.21, -20.07) * mm, v(4.28, -17.32) * mm, v(2.83, -16.08) * mm, v(1.59, -16.27) * mm], "startDerivative": vector(22.75, 3.8) * mm, "endDerivative": vector(-11.43, -4) * mm});
            skFitSpline(sketch, "E132.0", {"points": [v(-9.52, -20.38) * mm, v(-9.05, -20.3) * mm, v(-8.08, -20.14) * mm, v(-6.58, -19.95) * mm, v(-5.25, -19.88) * mm, v(-4.14, -19.91) * mm, v(-3.01, -20) * mm, v(-1.64, -20.18) * mm, v(-0.33, -20.34) * mm, v(0.62, -20.39) * mm, v(1.27, -20.38) * mm, v(1.86, -20.32) * mm, v(2.37, -20.2) * mm, v(2.79, -20.03) * mm, v(3.1, -19.84) * mm, v(3.26, -19.67) * mm, v(3.36, -19.52) * mm, v(3.45, -19.35) * mm, v(3.53, -19.07) * mm, v(3.57, -18.67) * mm, v(3.53, -18.26) * mm, v(3.42, -17.88) * mm, v(3.28, -17.59) * mm, v(3.09, -17.35) * mm, v(2.91, -17.2) * mm, v(2.79, -17.13) * mm, v(2.7, -17.1) * mm, v(2.64, -17.07) * mm, v(2.6, -17.07) * mm, v(2.54, -17.07) * mm, v(2.44, -17.08) * mm, v(2.25, -17.12) * mm, v(2.05, -17.2) * mm, v(1.93, -17.23) * mm]});
            skLineSegment(sketch, "E133", {"start": v(1.59, -16.27) * mm, "end": v(1.93, -17.23) * mm});
            skFitSpline(sketch, "E134", {"points": [v(-9.73, -21.96) * mm, v(-6.19, -21.5) * mm, v(-1.86, -21.76) * mm, v(0.17, -23.13) * mm, v(0.17, -24.97) * mm, v(-1.34, -25.82) * mm], "startDerivative": vector(14.62, 2.41) * mm, "endDerivative": vector(-11.29, -3.62) * mm});
            skFitSpline(sketch, "E135.0", {"points": [v(-9.56, -22.96) * mm, v(-8.95, -22.86) * mm, v(-8.06, -22.71) * mm, v(-6.8, -22.56) * mm, v(-5.8, -22.48) * mm, v(-4.75, -22.45) * mm, v(-3.7, -22.48) * mm, v(-2.73, -22.59) * mm, v(-1.9, -22.78) * mm, v(-1.27, -23.05) * mm, v(-0.94, -23.3) * mm, v(-0.78, -23.5) * mm, v(-0.7, -23.66) * mm, v(-0.64, -23.85) * mm, v(-0.61, -24.05) * mm, v(-0.62, -24.24) * mm, v(-0.65, -24.35) * mm, v(-0.68, -24.4) * mm, v(-0.69, -24.42) * mm, v(-0.7, -24.44) * mm, v(-0.74, -24.47) * mm, v(-0.83, -24.54) * mm, v(-1.03, -24.64) * mm, v(-1.31, -24.74) * mm, v(-1.53, -24.81) * mm, v(-1.65, -24.85) * mm]});
            skLineSegment(sketch, "E136", {"start": v(-1.65, -24.85) * mm, "end": v(-1.34, -25.82) * mm});
            skLineSegment(sketch, "E137.right", {"start": v(-8, -18.12) * mm, "end": v(-8, -19.13) * mm});
            skLineSegment(sketch, "E138.trimOffspring", {"start": v(-8, -20.14) * mm, "end": v(-8, -21.17) * mm});
            skLineSegment(sketch, "E139.trimOffspring", {"start": v(-8, -21.69) * mm, "end": v(-8, -22.71) * mm});
            skSolve(sketch);
        }
        {
            var Q0;
            Q0 = qSketchRegion(id + "F37", true);
            extrude(context, id + "F38", {"entities" : qUnion([Q0]), "operationType" : NewBodyOperationType.REMOVE, "oppositeDirection" : true, "depth" : 25.4 * mm, "offsetDistance" : 25.4 * mm});
        }
        {
            var Q0;
            Q0 = qSketchRegion(id + "F34", true);
            extrude(context, id + "F39", {"entities" : qUnion([Q0]), "operationType" : NewBodyOperationType.REMOVE, "oppositeDirection" : true, "depth" : 25.4 * mm, "offsetDistance" : 25.4 * mm});
        }
    });
